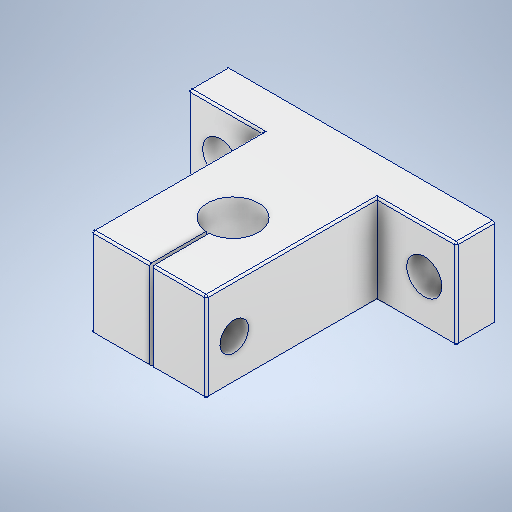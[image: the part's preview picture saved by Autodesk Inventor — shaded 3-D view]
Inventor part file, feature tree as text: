
AUTODESK INVENTOR PART (.ipt)
format: ipt  version: 2025.2 (Build 292293000, 293)  size: 304,128 bytes
history: native  units: mm
features: sketch x4, extrude x3, other x1, fillet x1
ambient origin geometry x8: Origin, YZ Plane, XZ Plane, XY Plane, X Axis, Y Axis, Z Axis, Center Point
bodies: Body1 (feature_tree)
feature tree (9):
  other  "Sólido1"
  extrude  "Extrusión1"  Depth=5.5mm
  sketch  "Boceto2"  dims[d2=16.0mm d3=32.0mm d4=14.0mm]
  extrude  "Extrusión2"  Depth=14.0mm
  fillet  "Empalme1"  Radius=14.0mm
  extrude  "Extrusión3"  Depth=6.0mm TaperAngle=0.0deg
  sketch  "Boceto1"  dims[d0=5.5mm d1=5.5mm]
  sketch  "Boceto3"  dims[d5=42.0mm d6=6.0mm d7=0.0mm]
  sketch  "Boceto5"  dims[d8=32.8mm d9=8.0mm d10=20.0mm d12=18.0mm d13=0.5mm d14=14.0mm d15=14.0mm d16=0.0mm d17=0.3mm d18=4.5mm d19=28.4mm d20=20.0mm d21=0.0mm]
